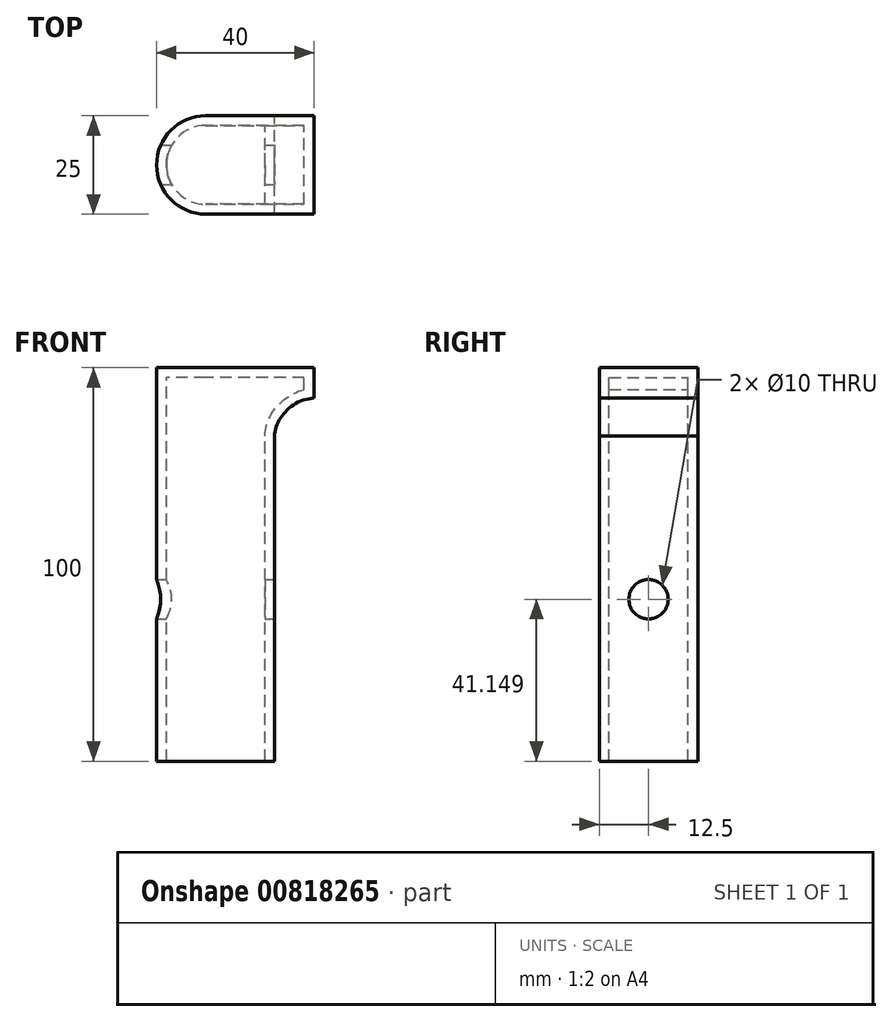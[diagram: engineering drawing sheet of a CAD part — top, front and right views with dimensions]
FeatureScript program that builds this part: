
annotation { "Feature Type Name" : "Feature", "Feature Type Description" : "" }
export const myFeature = defineFeature(function(context is Context, id is Id, definition is map)
    precondition{}
    {
        {
            var Q0;
            Q0=qCreatedBy(makeId("Front.planeOp"),FACE);
            var sketch = newSketch(context, id + "F0", { "sketchPlane" : qUnion([Q0])});
            skLineSegment(sketch, "E0", {"start": v(-12.5, 30.37) * mm, "end": v(-12.5, -69.63) * mm});
            skLineSegment(sketch, "E1", {"start": v(-12.5, -69.63) * mm, "end": v(17.5, -69.63) * mm});
            skLineSegment(sketch, "E2", {"start": v(17.5, -69.63) * mm, "end": v(17.5, 12.96) * mm});
            skLineSegment(sketch, "E3", {"start": v(27.5, 22.6) * mm, "end": v(27.5, 30.37) * mm});
            skLineSegment(sketch, "E4", {"start": v(27.5, 30.37) * mm, "end": v(-12.5, 30.37) * mm});
            skFitSpline(sketch, "E5", {"points": [v(17.5, 12.96) * mm, v(27.5, 22.6) * mm], "startDerivative": vector(0.2, 13.13) * mm, "endDerivative": vector(16.7, 0.41) * mm});
            skLineSegment(sketch, "E6", {"start": v(0, 30.37) * mm, "end": v(0, -69.63) * mm});
            skLineSegment(sketch, "E7", {"start": v(-12.5, -36.2) * mm, "end": v(17.5, -28.33) * mm});
            skSolve(sketch);
        }
        {
            var Q0;
            {var subQ2=sQuery(id+"F0.wireOp",EDGE,"E3");Q0=makeQuery(id+"F0.imprint","IMPRINT",FACE,{"disambiguationData":[TD([[makeQuery(id+"F0.imprint","IMPRINT",EDGE,{"derivedFrom":subQ2}),1.0]])]});}
            var Q1;
            {var subQ0=sQuery(id+"F0.wireOp",EDGE,"E2");var subQ1=sQuery(id+"F0.wireOp",EDGE,"E1");var subQ2=makeQuery(id+"F0.imprint","INTERSECT",VERTEX,{"derivedFrom":[subQ1,subQ0]});Q1=makeQuery(id+"F0.imprint","IMPRINT",FACE,{"disambiguationData":[TD([[makeQuery(id+"F0.imprint","IMPRINT",EDGE,{"disambiguationData":[TD([[subQ2,1.0]])],"derivedFrom":subQ1}),1.0]])]});}
            extrude(context, id + "F1", {"entities" : qUnion([Q0, Q1]), "endBound" : BoundingType.SYMMETRIC, "depth" : 25 * mm, "offsetDistance" : 25 * mm});
        }
        {
            var Q0;
            {var subQ0=sQuery(id+"F0.wireOp",EDGE,"E1");var subQ1=sQuery(id+"F0.wireOp",EDGE,"E0");var subQ2=makeQuery(id+"F0.imprint","INTERSECT",VERTEX,{"derivedFrom":[subQ1,subQ0]});Q0=makeQuery(id+"F0.imprint","IMPRINT",FACE,{"disambiguationData":[TD([[makeQuery(id+"F0.imprint","IMPRINT",EDGE,{"disambiguationData":[TD([[subQ2,1.0]])],"derivedFrom":subQ1}),1.0]])]});}
            var Q1;
            {var subQ0=sQuery(id+"F0.wireOp",EDGE,"E4");var subQ1=sQuery(id+"F0.wireOp",EDGE,"E0");var subQ2=makeQuery(id+"F0.imprint","INTERSECT",VERTEX,{"derivedFrom":[subQ1,subQ0]});Q1=makeQuery(id+"F0.imprint","IMPRINT",FACE,{"disambiguationData":[TD([[makeQuery(id+"F0.imprint","IMPRINT",EDGE,{"disambiguationData":[TD([[subQ2,-1.0]])],"derivedFrom":subQ1}),1.0]])]});}
            var Q2;
            Q2=sQuery(id+"F0.wireOp",EDGE,"E6");
            revolve(context, id + "F2", {"operationType" : NewBodyOperationType.ADD, "surfaceOperationType" : NewSurfaceOperationType.NEW, "entities" : qUnion([Q0, Q1]), "axis" : qUnion([Q2]), "revolveType" : RevolveType.FULL});
        }
        {
            var Q0;
            {var subQ0=sQuery(id+"F0.wireOp",EDGE,"E1");Q0=makeQuery(id+"F2.boolean.opBoolean","MERGE",FACE,{"derivedFrom":[makeQuery(id+"F1.opExtrude","SWEPT_FACE",FACE,{"disambiguationData":[OSD([subQ0])]}),makeQuery(id+"F2.opRevolve","SWEPT_FACE",FACE,{"disambiguationData":[OSD([subQ0])]})]});}
            shell(context, id + "F3", {"entities" : qUnion([Q0]), "thickness" : 2.5 * mm});
        }
        {
            var Q0;
            Q0=makeQuery(id+"F1.opExtrude","SWEPT_FACE",FACE,{"disambiguationData":[OSD([sQuery(id+"F0.wireOp",EDGE,"E2")])]});
            var sketch = newSketch(context, id + "F4", { "sketchPlane" : qUnion([Q0])});
            skCircle(sketch, "E8", {"center": v(0, -28.33) * mm, "radius": 5 * mm});
            skSolve(sketch);
        }
        {
            var Q0;
            Q0=makeQuery(id+"F4.imprint","IMPRINT",FACE,{"disambiguationData":[TD([[makeQuery(id+"F4.imprint","IMPRINT",EDGE,{"derivedFrom":sQuery(id+"F4.wireOp",EDGE,"E8")}),1.0]])]});
            var sketch = newSketch(context, id + "F5", { "sketchPlane" : qUnion([Q0])});
            skPoint(sketch, "E9", {"position": v(0, -28.48) * mm});
            skSolve(sketch);
        }
        {
            var Q0;
            Q0=sQuery(id+"F5.wireOp",VERTEX,"E9");
            var Q1;
            Q1=makeQuery(id+"F1.opExtrude","SWEPT_BODY",BODY,{"disambiguationData":[OSD([sQuery(id+"F0.wireOp",EDGE,"E1"),sQuery(id+"F0.wireOp",EDGE,"E2"),sQuery(id+"F0.wireOp",EDGE,"E3"),sQuery(id+"F0.wireOp",EDGE,"E4"),sQuery(id+"F0.wireOp",EDGE,"E5"),sQuery(id+"F0.wireOp",EDGE,"E6")])]});
            hole(context, id + "F6", {"style" : HoleStyle.SIMPLE, "endStyle" : HoleEndStyle.THROUGH, "holeDiameter" : 10 * mm, "majorDiameter" : 5 * mm, "isTappedThrough" : true, "tappedDepth" : 12 * mm, "tapClearance" : 3, "locations" : qUnion([Q0]), "scope" : qUnion([Q1])});
        }
    });
